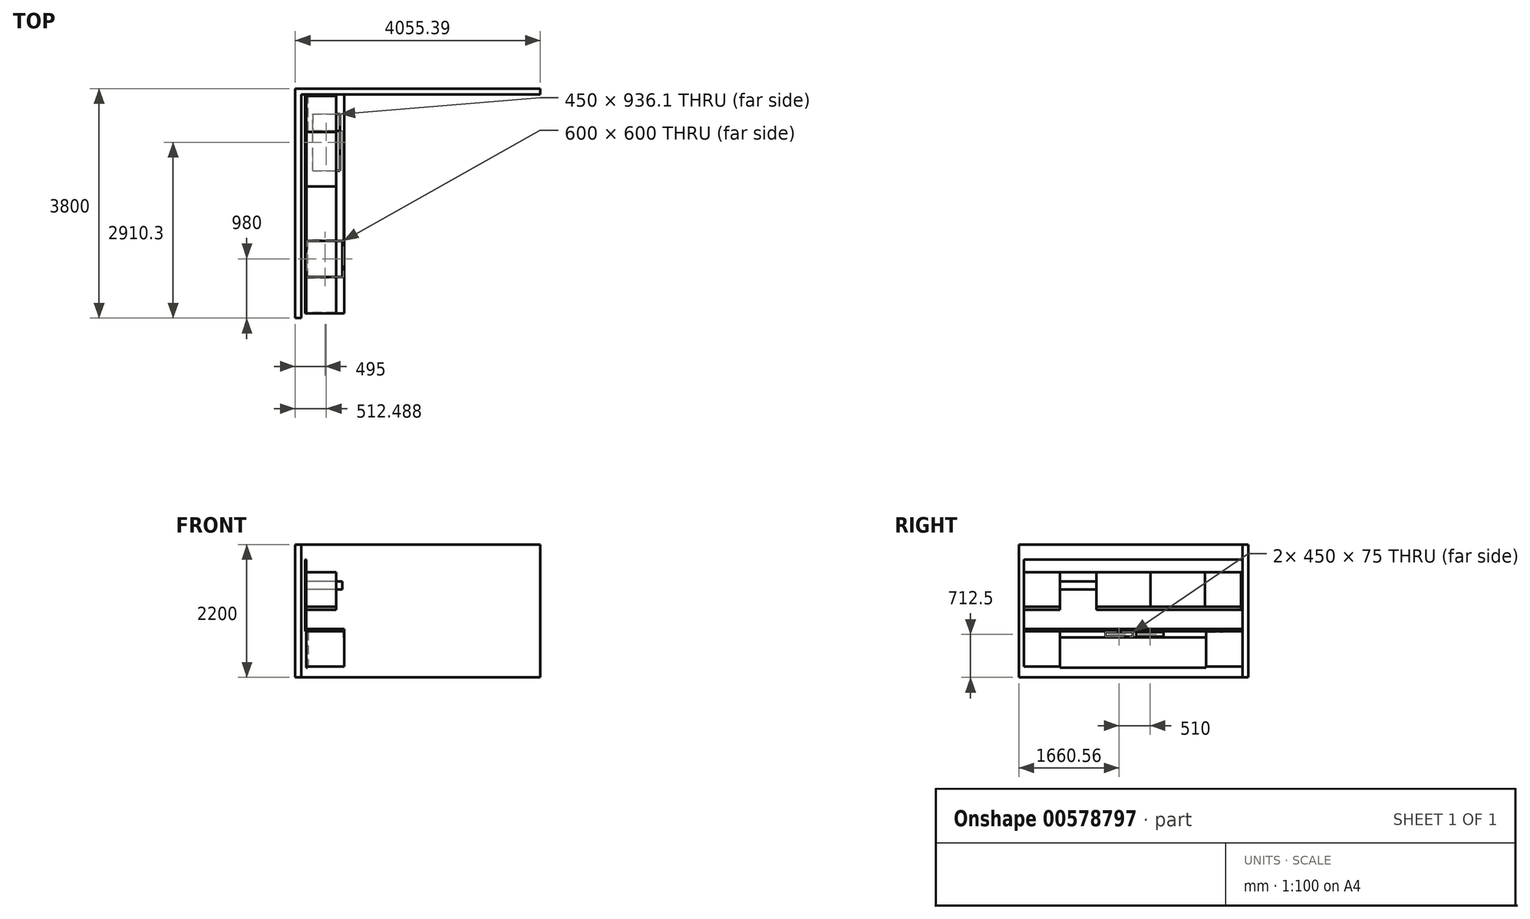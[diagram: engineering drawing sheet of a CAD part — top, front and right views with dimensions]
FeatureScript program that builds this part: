
annotation { "Feature Type Name" : "Feature", "Feature Type Description" : "" }
export const myFeature = defineFeature(function(context is Context, id is Id, definition is map)
    precondition{}
    {
        {
            var Q0;
            Q0=qCreatedBy(makeId("Top.planeOp"),FACE);
            var sketch = newSketch(context, id + "F0", { "sketchPlane" : qUnion([Q0])});
            skLineSegment(sketch, "E0.bottom", {"start": v(0, 0) * mm, "end": v(-100, 0) * mm});
            skLineSegment(sketch, "E0.top", {"start": v(0, -3700) * mm, "end": v(-100, -3700) * mm});
            skLineSegment(sketch, "E0.left", {"start": v(0, 0) * mm, "end": v(0, -3700) * mm});
            skLineSegment(sketch, "E0.right", {"start": v(-100, 0) * mm, "end": v(-100, -3700) * mm});
            skLineSegment(sketch, "E1.bottom", {"start": v(-100, 0) * mm, "end": v(3955.39, 0) * mm});
            skLineSegment(sketch, "E1.top", {"start": v(-100, 100) * mm, "end": v(3955.39, 100) * mm});
            skLineSegment(sketch, "E1.left", {"start": v(-100, 0) * mm, "end": v(-100, 100) * mm});
            skLineSegment(sketch, "E1.right", {"start": v(3955.39, 0) * mm, "end": v(3955.39, 100) * mm});
            skSolve(sketch);
        }
        {
            var Q0;
            Q0=makeQuery(id+"F0.imprint","IMPRINT",FACE,{"disambiguationData":[TD([[makeQuery(id+"F0.imprint","IMPRINT",EDGE,{"derivedFrom":sQuery(id+"F0.wireOp",EDGE,"E0.top")}),-1.0]])]});
            var Q1;
            Q1=makeQuery(id+"F0.imprint","IMPRINT",FACE,{"disambiguationData":[TD([[makeQuery(id+"F0.imprint","IMPRINT",EDGE,{"derivedFrom":sQuery(id+"F0.wireOp",EDGE,"E1.top")}),-1.0]])]});
            extrude(context, id + "F1", {"entities" : qUnion([Q0, Q1]), "depth" : 2200 * mm, "offsetDistance" : 25 * mm});
        }
        {
            var Q0;
            Q0=makeQuery(id+"F1.opExtrude","SWEPT_FACE",FACE,{"disambiguationData":[OSD([sQuery(id+"F0.wireOp",EDGE,"E1.bottom")])]});
            var sketch = newSketch(context, id + "F2", { "sketchPlane" : qUnion([Q0])});
            skLineSegment(sketch, "E2.bottom", {"start": v(60, 800) * mm, "end": v(710, 800) * mm});
            skLineSegment(sketch, "E2.top", {"start": v(60, 760) * mm, "end": v(710, 760) * mm});
            skLineSegment(sketch, "E2.left", {"start": v(60, 800) * mm, "end": v(60, 760) * mm});
            skLineSegment(sketch, "E2.right", {"start": v(710, 800) * mm, "end": v(710, 760) * mm});
            skSolve(sketch);
        }
        {
            var Q0;
            Q0 = qSketchRegion(id + "F2", true);
            extrude(context, id + "F3", {"entities" : qUnion([Q0]), "depth" : 3620 * mm, "offsetDistance" : 25 * mm});
        }
        {
            var Q0;
            Q0=makeQuery(id+"F3.opExtrude","SWEPT_FACE",FACE,{"disambiguationData":[OSD([sQuery(id+"F2.wireOp",EDGE,"E2.bottom")])]});
            var sketch = newSketch(context, id + "F4", { "sketchPlane" : qUnion([Q0])});
            skLineSegment(sketch, "E3.bottom", {"start": v(60, -3620) * mm, "end": v(78, -3620) * mm});
            skLineSegment(sketch, "E3.top", {"start": v(60, 0) * mm, "end": v(78, 0) * mm});
            skLineSegment(sketch, "E3.left", {"start": v(60, -3620) * mm, "end": v(60, 0) * mm});
            skLineSegment(sketch, "E3.right", {"start": v(78, -3620) * mm, "end": v(78, 0) * mm});
            skSolve(sketch);
        }
        {
            var Q0;
            Q0=makeQuery(id+"F4.imprint","IMPRINT",FACE,{"disambiguationData":[TD([[makeQuery(id+"F4.imprint","IMPRINT",EDGE,{"derivedFrom":sQuery(id+"F4.wireOp",EDGE,"E3.bottom")}),1.0]])]});
            extrude(context, id + "F5", {"entities" : qUnion([Q0]), "depth" : 1150 * mm, "offsetDistance" : 25 * mm});
        }
        {
            var Q0;
            Q0=makeQuery(id+"F5.opExtrude","SWEPT_FACE",FACE,{"disambiguationData":[OSD([sQuery(id+"F4.wireOp",EDGE,"E3.right")])]});
            var sketch = newSketch(context, id + "F6", { "sketchPlane" : qUnion([Q0])});
            skLineSegment(sketch, "E4.bottom", {"start": v(-3620, 1740) * mm, "end": v(-3020, 1740) * mm});
            skLineSegment(sketch, "E4.top", {"start": v(-3620, 1170) * mm, "end": v(-3020, 1170) * mm});
            skLineSegment(sketch, "E4.left", {"start": v(-3620, 1740) * mm, "end": v(-3620, 1170) * mm});
            skLineSegment(sketch, "E4.right", {"start": v(-3020, 1740) * mm, "end": v(-3020, 1170) * mm});
            skLineSegment(sketch, "E5.bottom", {"start": v(-3020, 1740) * mm, "end": v(-2420, 1740) * mm});
            skLineSegment(sketch, "E5.top", {"start": v(-3020, 1590) * mm, "end": v(-2420, 1590) * mm});
            skLineSegment(sketch, "E5.left", {"start": v(-3020, 1740) * mm, "end": v(-3020, 1590) * mm});
            skLineSegment(sketch, "E5.right", {"start": v(-2420, 1740) * mm, "end": v(-2420, 1590) * mm});
            skLineSegment(sketch, "E6.bottom", {"start": v(-2420, 1740) * mm, "end": v(-1520, 1740) * mm});
            skLineSegment(sketch, "E6.top", {"start": v(-2420, 1170) * mm, "end": v(-1520, 1170) * mm});
            skLineSegment(sketch, "E6.left", {"start": v(-2420, 1740) * mm, "end": v(-2420, 1170) * mm});
            skLineSegment(sketch, "E6.right", {"start": v(-1520, 1740) * mm, "end": v(-1520, 1170) * mm});
            skLineSegment(sketch, "E7.bottom", {"start": v(-1520, 1740) * mm, "end": v(-620, 1740) * mm});
            skLineSegment(sketch, "E7.top", {"start": v(-1520, 1170) * mm, "end": v(-620, 1170) * mm});
            skLineSegment(sketch, "E7.right", {"start": v(-620, 1740) * mm, "end": v(-620, 1170) * mm});
            skLineSegment(sketch, "E8.bottom", {"start": v(-620, 1740) * mm, "end": v(-20, 1740) * mm});
            skLineSegment(sketch, "E8.top", {"start": v(-620, 1170) * mm, "end": v(-20, 1170) * mm});
            skLineSegment(sketch, "E8.right", {"start": v(-20, 1740) * mm, "end": v(-20, 1170) * mm});
            skLineSegment(sketch, "E9.top", {"start": v(-3020, 1455) * mm, "end": v(-2420, 1455) * mm});
            skLineSegment(sketch, "E9.left", {"start": v(-3020, 1590) * mm, "end": v(-3020, 1455) * mm});
            skLineSegment(sketch, "E9.right", {"start": v(-2420, 1590) * mm, "end": v(-2420, 1455) * mm});
            skSolve(sketch);
        }
        {
            var Q0;
            {var subQ1=sQuery(id+"F6.wireOp",EDGE,"E4.bottom");Q0=makeQuery(id+"F6.imprint","IMPRINT",FACE,{"disambiguationData":[TD([[makeQuery(id+"F6.imprint","IMPRINT",EDGE,{"derivedFrom":subQ1}),-1.0]])]});}
            extrude(context, id + "F7", {"entities" : qUnion([Q0]), "depth" : 500 * mm, "offsetDistance" : 25 * mm});
        }
        {
            var Q0;
            Q0=makeQuery(id+"F6.imprint","IMPRINT",FACE,{"disambiguationData":[TD([[makeQuery(id+"F6.imprint","IMPRINT",EDGE,{"derivedFrom":sQuery(id+"F6.wireOp",EDGE,"E7.bottom")}),-1.0]])]});
            extrude(context, id + "F8", {"entities" : qUnion([Q0]), "depth" : 500 * mm, "offsetDistance" : 25 * mm});
        }
        {
            var Q0;
            {var subQ3=sQuery(id+"F6.wireOp",EDGE,"E6.bottom");Q0=makeQuery(id+"F6.imprint","IMPRINT",FACE,{"disambiguationData":[TD([[makeQuery(id+"F6.imprint","IMPRINT",EDGE,{"derivedFrom":subQ3}),-1.0]])]});}
            extrude(context, id + "F9", {"entities" : qUnion([Q0]), "depth" : 500 * mm, "offsetDistance" : 25 * mm});
        }
        {
            var Q0;
            Q0=makeQuery(id+"F6.imprint","IMPRINT",FACE,{"disambiguationData":[TD([[makeQuery(id+"F6.imprint","IMPRINT",EDGE,{"derivedFrom":sQuery(id+"F6.wireOp",EDGE,"E8.bottom")}),-1.0]])]});
            extrude(context, id + "F10", {"entities" : qUnion([Q0]), "depth" : 500 * mm, "offsetDistance" : 25 * mm});
        }
        {
            var Q0;
            Q0=makeQuery(id+"F3.opExtrude","SWEPT_FACE",FACE,{"disambiguationData":[OSD([sQuery(id+"F2.wireOp",EDGE,"E2.right")])]});
            var sketch = newSketch(context, id + "F11", { "sketchPlane" : qUnion([Q0])});
            skLineSegment(sketch, "E10.bottom", {"start": v(-3620, 760) * mm, "end": v(-3020, 760) * mm});
            skLineSegment(sketch, "E10.top", {"start": v(-3620, 180) * mm, "end": v(-3020, 180) * mm});
            skLineSegment(sketch, "E10.left", {"start": v(-3620, 760) * mm, "end": v(-3620, 180) * mm});
            skLineSegment(sketch, "E10.right", {"start": v(-3020, 760) * mm, "end": v(-3020, 180) * mm});
            skLineSegment(sketch, "E11.bottom", {"start": v(0, 760) * mm, "end": v(-600, 760) * mm});
            skLineSegment(sketch, "E11.top", {"start": v(0, 180) * mm, "end": v(-600, 180) * mm});
            skLineSegment(sketch, "E11.left", {"start": v(0, 760) * mm, "end": v(0, 180) * mm});
            skLineSegment(sketch, "E11.right", {"start": v(-600, 760) * mm, "end": v(-600, 180) * mm});
            skLineSegment(sketch, "E12.bottom", {"start": v(-3020, 760) * mm, "end": v(-600, 760) * mm});
            skLineSegment(sketch, "E12.top", {"start": v(-3020, 660) * mm, "end": v(-600, 660) * mm});
            skLineSegment(sketch, "E12.left", {"start": v(-3020, 760) * mm, "end": v(-3020, 660) * mm});
            skLineSegment(sketch, "E12.right", {"start": v(-600, 760) * mm, "end": v(-600, 660) * mm});
            skSolve(sketch);
        }
        {
            var Q0;
            Q0=makeQuery(id+"F11.imprint","IMPRINT",FACE,{"disambiguationData":[TD([[makeQuery(id+"F11.imprint","IMPRINT",EDGE,{"derivedFrom":sQuery(id+"F11.wireOp",EDGE,"E10.bottom")}),-1.0]])]});
            extrude(context, id + "F12", {"entities" : qUnion([Q0]), "oppositeDirection" : true, "depth" : 630 * mm, "offsetDistance" : 25 * mm});
        }
        {
            var Q0;
            Q0=makeQuery(id+"F11.imprint","IMPRINT",FACE,{"disambiguationData":[TD([[makeQuery(id+"F11.imprint","IMPRINT",EDGE,{"derivedFrom":sQuery(id+"F11.wireOp",EDGE,"E11.bottom")}),-1.0]])]});
            extrude(context, id + "F13", {"entities" : qUnion([Q0]), "oppositeDirection" : true, "depth" : 600 * mm, "offsetDistance" : 25 * mm});
        }
        {
            var Q0;
            Q0=makeQuery(id+"F11.imprint","IMPRINT",FACE,{"disambiguationData":[TD([[makeQuery(id+"F11.imprint","IMPRINT",EDGE,{"derivedFrom":sQuery(id+"F11.wireOp",EDGE,"E12.bottom")}),-1.0]])]});
            extrude(context, id + "F14", {"entities" : qUnion([Q0]), "oppositeDirection" : true, "depth" : 18 * mm, "offsetDistance" : 25 * mm});
        }
        {
            var Q0;
            Q0=makeQuery(id+"F3.opExtrude","SWEPT_FACE",FACE,{"disambiguationData":[OSD([sQuery(id+"F2.wireOp",EDGE,"E2.top")])]});
            var sketch = newSketch(context, id + "F15", { "sketchPlane" : qUnion([Q0])});
            skLineSegment(sketch, "E13.bottom", {"start": v(80, 3020) * mm, "end": v(98, 3020) * mm});
            skLineSegment(sketch, "E13.top", {"start": v(80, 600) * mm, "end": v(98, 600) * mm});
            skLineSegment(sketch, "E13.left", {"start": v(80, 3020) * mm, "end": v(80, 600) * mm});
            skLineSegment(sketch, "E13.right", {"start": v(98, 3020) * mm, "end": v(98, 600) * mm});
            skSolve(sketch);
        }
        {
            var Q0;
            Q0 = qSketchRegion(id + "F15", true);
            extrude(context, id + "F16", {"entities" : qUnion([Q0]), "depth" : 600 * mm, "offsetDistance" : 25 * mm});
        }
        {
            var Q0;
            {var subQ0=sQuery(id+"F6.wireOp",EDGE,"E5.bottom");Q0=makeQuery(id+"F6.imprint","IMPRINT",FACE,{"disambiguationData":[TD([[makeQuery(id+"F6.imprint","IMPRINT",EDGE,{"derivedFrom":subQ0}),-1.0]])]});}
            extrude(context, id + "F17", {"entities" : qUnion([Q0]), "depth" : 500 * mm, "offsetDistance" : 25 * mm});
        }
        {
            var Q0;
            Q0=makeQuery(id+"F6.imprint","IMPRINT",FACE,{"disambiguationData":[TD([[makeQuery(id+"F6.imprint","IMPRINT",EDGE,{"derivedFrom":sQuery(id+"F6.wireOp",EDGE,"E5.top")}),-1.0]])]});
            extrude(context, id + "F18", {"entities" : qUnion([Q0]), "depth" : 600 * mm, "offsetDistance" : 25 * mm});
        }
        {
            var Q0;
            Q0=makeQuery(id+"F7.opExtrude","SWEPT_FACE",FACE,{"disambiguationData":[OSD([sQuery(id+"F6.wireOp",EDGE,"E4.top")])]});
            var sketch = newSketch(context, id + "F19", { "sketchPlane" : qUnion([Q0])});
            skLineSegment(sketch, "E14", {"start": v(78, 3620) * mm, "end": v(578, 3620) * mm});
            skLineSegment(sketch, "E15", {"start": v(578, 3620) * mm, "end": v(578, 3020) * mm});
            skLineSegment(sketch, "E16", {"start": v(578, 3020) * mm, "end": v(78, 3020) * mm});
            skLineSegment(sketch, "E17", {"start": v(78, 3020) * mm, "end": v(78, 3030) * mm});
            skLineSegment(sketch, "E18", {"start": v(78, 3030) * mm, "end": v(568, 3030) * mm});
            skLineSegment(sketch, "E19", {"start": v(568, 3030) * mm, "end": v(568, 3610) * mm});
            skLineSegment(sketch, "E20", {"start": v(568, 3610) * mm, "end": v(78, 3610) * mm});
            skLineSegment(sketch, "E21", {"start": v(78, 3610) * mm, "end": v(78, 3620) * mm});
            skSolve(sketch);
        }
        {
            var Q0;
            Q0 = qSketchRegion(id + "F19", true);
            extrude(context, id + "F20", {"entities" : qUnion([Q0]), "depth" : 50 * mm, "offsetDistance" : 25 * mm});
        }
        {
            var Q0;
            Q0=makeQuery(id+"F9.opExtrude","SWEPT_FACE",FACE,{"disambiguationData":[OSD([sQuery(id+"F6.wireOp",EDGE,"E6.top")])]});
            var sketch = newSketch(context, id + "F21", { "sketchPlane" : qUnion([Q0])});
            skLineSegment(sketch, "E22", {"start": v(78, 2420) * mm, "end": v(578, 2420) * mm});
            skLineSegment(sketch, "E23", {"start": v(578, 2420) * mm, "end": v(578, 20) * mm});
            skLineSegment(sketch, "E24", {"start": v(578, 20) * mm, "end": v(78, 20) * mm});
            skLineSegment(sketch, "E25", {"start": v(78, 20) * mm, "end": v(78, 30) * mm});
            skLineSegment(sketch, "E26", {"start": v(78, 30) * mm, "end": v(568, 30) * mm});
            skLineSegment(sketch, "E27", {"start": v(568, 30) * mm, "end": v(568, 2410) * mm});
            skLineSegment(sketch, "E28", {"start": v(568, 2410) * mm, "end": v(78, 2410) * mm});
            skLineSegment(sketch, "E29", {"start": v(78, 2410) * mm, "end": v(78, 2420) * mm});
            skSolve(sketch);
        }
        {
            var Q0;
            Q0 = qSketchRegion(id + "F21", true);
            extrude(context, id + "F22", {"entities" : qUnion([Q0]), "depth" : 50 * mm, "offsetDistance" : 25 * mm});
        }
        {
            var Q0;
            Q0=makeQuery(id+"F11.imprint","IMPRINT",FACE,{"disambiguationData":[TD([[makeQuery(id+"F11.imprint","IMPRINT",EDGE,{"derivedFrom":sQuery(id+"F11.wireOp",EDGE,"E12.bottom")}),-1.0]])]});
            var sketch = newSketch(context, id + "F23", { "sketchPlane" : qUnion([Q0])});
            skLineSegment(sketch, "E30.bottom", {"start": v(-2264.44, 750) * mm, "end": v(-1814.44, 750) * mm});
            skLineSegment(sketch, "E30.top", {"start": v(-2264.44, 675) * mm, "end": v(-1814.44, 675) * mm});
            skLineSegment(sketch, "E30.left", {"start": v(-2264.44, 750) * mm, "end": v(-2264.44, 675) * mm});
            skLineSegment(sketch, "E30.right", {"start": v(-1814.44, 750) * mm, "end": v(-1814.44, 675) * mm});
            skLineSegment(sketch, "E31.bottom", {"start": v(-1754.44, 750) * mm, "end": v(-1304.44, 750) * mm});
            skLineSegment(sketch, "E31.top", {"start": v(-1754.44, 675) * mm, "end": v(-1304.44, 675) * mm});
            skLineSegment(sketch, "E31.left", {"start": v(-1754.44, 750) * mm, "end": v(-1754.44, 675) * mm});
            skLineSegment(sketch, "E31.right", {"start": v(-1304.44, 750) * mm, "end": v(-1304.44, 675) * mm});
            skSolve(sketch);
        }
        {
            var Q0;
            Q0=makeQuery(id+"F23.imprint","IMPRINT",FACE,{"disambiguationData":[TD([[makeQuery(id+"F23.imprint","IMPRINT",EDGE,{"derivedFrom":sQuery(id+"F23.wireOp",EDGE,"E31.bottom")}),-1.0]])]});
            var Q1;
            Q1=makeQuery(id+"F23.imprint","IMPRINT",FACE,{"disambiguationData":[TD([[makeQuery(id+"F23.imprint","IMPRINT",EDGE,{"derivedFrom":sQuery(id+"F23.wireOp",EDGE,"E30.bottom")}),-1.0]])]});
            extrude(context, id + "F24", {"entities" : qUnion([Q0, Q1]), "operationType" : NewBodyOperationType.REMOVE, "oppositeDirection" : true, "depth" : 25 * mm, "offsetDistance" : 25 * mm});
        }
        {
            var Q0;
            Q0=makeQuery(id+"F3.opExtrude","SWEPT_FACE",FACE,{"disambiguationData":[OSD([sQuery(id+"F2.wireOp",EDGE,"E2.bottom")])]});
            var sketch = newSketch(context, id + "F25", { "sketchPlane" : qUnion([Q0])});
            skLineSegment(sketch, "E32.bottom", {"start": v(695, -2420) * mm, "end": v(95, -2420) * mm});
            skLineSegment(sketch, "E32.top", {"start": v(695, -3020) * mm, "end": v(95, -3020) * mm});
            skLineSegment(sketch, "E32.left", {"start": v(695, -2420) * mm, "end": v(695, -3020) * mm});
            skLineSegment(sketch, "E32.right", {"start": v(95, -2420) * mm, "end": v(95, -3020) * mm});
            skPoint(sketch, "E32.middle", {"position": v(395, -2720) * mm});
            skLineSegment(sketch, "E33.bottom", {"start": v(187.49, -1257.76) * mm, "end": v(637.49, -1257.76) * mm});
            skLineSegment(sketch, "E33.top", {"start": v(187.49, -321.65) * mm, "end": v(637.49, -321.65) * mm});
            skLineSegment(sketch, "E33.left", {"start": v(187.49, -1257.76) * mm, "end": v(187.49, -321.65) * mm});
            skLineSegment(sketch, "E33.right", {"start": v(637.49, -1257.76) * mm, "end": v(637.49, -321.65) * mm});
            skPoint(sketch, "E33.middle", {"position": v(412.49, -789.7) * mm});
            skLineSegment(sketch, "E34.bottom", {"start": v(187.49, -771.65) * mm, "end": v(637.49, -771.65) * mm});
            skLineSegment(sketch, "E34.top", {"start": v(187.49, -807.76) * mm, "end": v(637.49, -807.76) * mm});
            skLineSegment(sketch, "E34.left", {"start": v(187.49, -771.65) * mm, "end": v(187.49, -807.76) * mm});
            skLineSegment(sketch, "E34.right", {"start": v(637.49, -771.65) * mm, "end": v(637.49, -807.76) * mm});
            skSolve(sketch);
        }
        {
            var Q0;
            Q0 = qSketchRegion(id + "F25", true);
            extrude(context, id + "F26", {"entities" : qUnion([Q0]), "operationType" : NewBodyOperationType.REMOVE, "oppositeDirection" : true, "depth" : 50 * mm, "offsetDistance" : 25 * mm});
        }
    });
